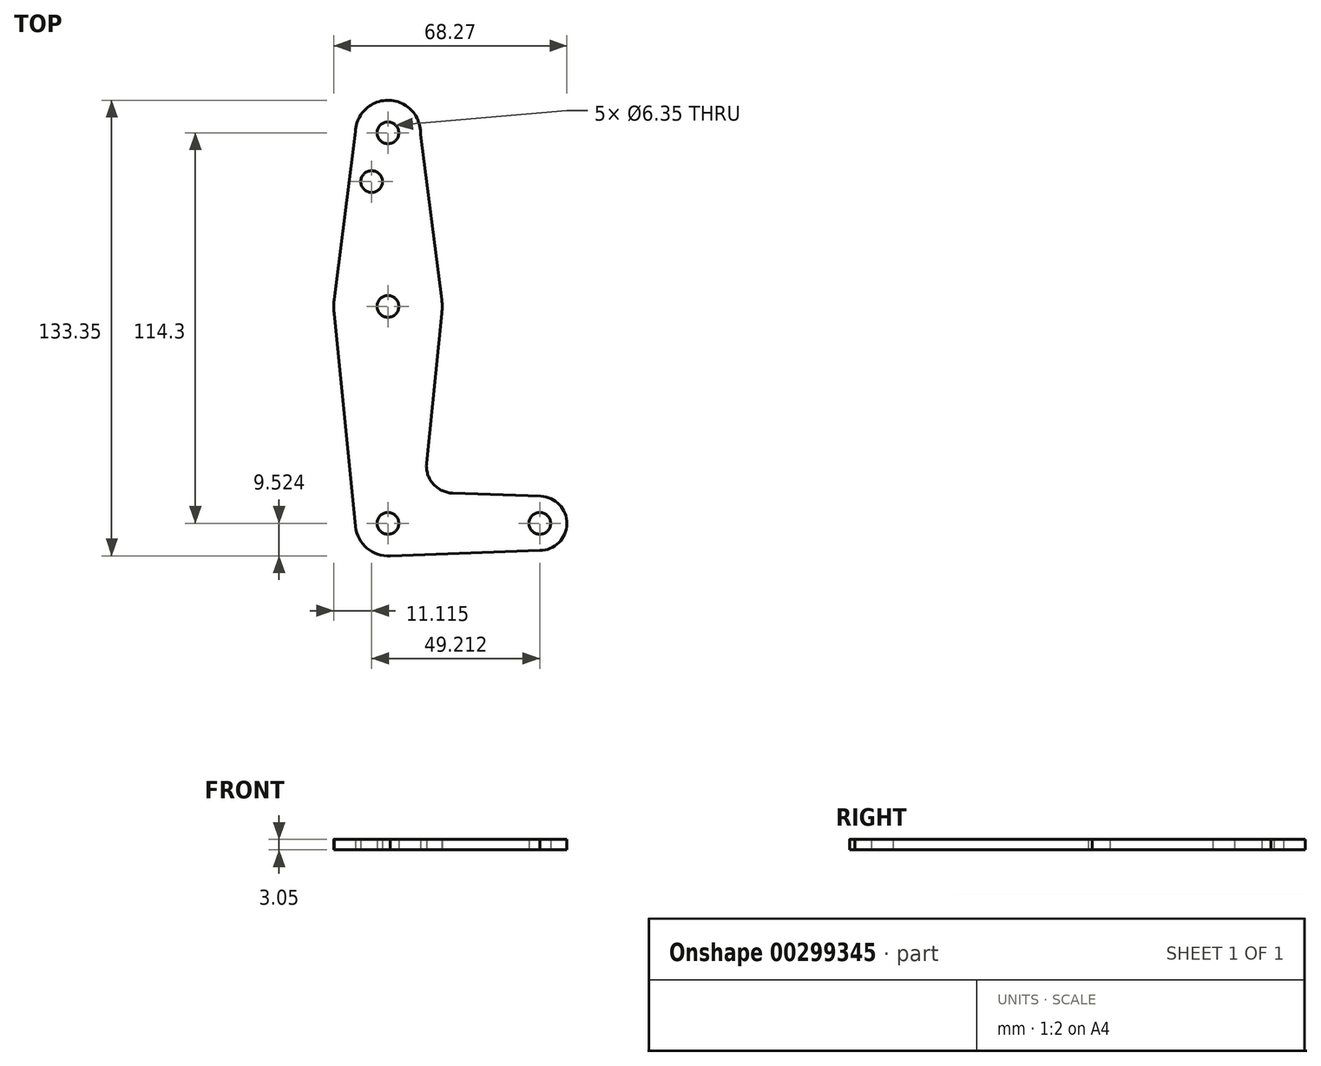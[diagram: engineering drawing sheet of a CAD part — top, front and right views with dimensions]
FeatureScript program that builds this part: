
annotation { "Feature Type Name" : "Feature", "Feature Type Description" : "" }
export const myFeature = defineFeature(function(context is Context, id is Id, definition is map)
    precondition{}
    {
        {
            var Q0;
            Q0=qCreatedBy(makeId("Top.planeOp"),FACE);
            var sketch = newSketch(context, id + "F0", { "sketchPlane" : qUnion([Q0])});
            skLineSegment(sketch, "E0", {"start": v(-11.27, 77.32) * mm, "end": v(-11.27, -36.98) * mm, "construction": true});
            skLineSegment(sketch, "E1", {"start": v(-11.27, -36.98) * mm, "end": v(33.18, -36.98) * mm, "construction": true});
            skCircle(sketch, "E2", {"center": v(-11.27, 77.32) * mm, "radius": 9.53 * mm});
            skCircle(sketch, "E3", {"center": v(-11.27, 26.52) * mm, "radius": 15.88 * mm});
            skCircle(sketch, "E4", {"center": v(-11.27, -36.98) * mm, "radius": 9.53 * mm});
            skCircle(sketch, "E5", {"center": v(33.18, -36.98) * mm, "radius": 7.94 * mm});
            skLineSegment(sketch, "E6", {"start": v(-11.27, -46.5) * mm, "end": v(33.18, -44.91) * mm});
            skCircle(sketch, "E7", {"center": v(-11.27, 77.32) * mm, "radius": 3.18 * mm});
            skCircle(sketch, "E8", {"center": v(-11.27, 26.52) * mm, "radius": 3.18 * mm});
            skCircle(sketch, "E9", {"center": v(-11.27, -36.98) * mm, "radius": 3.18 * mm});
            skCircle(sketch, "E10", {"center": v(33.18, -36.98) * mm, "radius": 3.18 * mm});
            skCircle(sketch, "E11", {"center": v(-16.03, 63.05) * mm, "radius": 3.18 * mm});
            skPoint(sketch, "E12.newPointA", {"position": v(0, -26.21) * mm});
            skLineSegment(sketch, "E13", {"start": v(-1.76, 76.8) * mm, "end": v(4.47, 28.56) * mm});
            skLineSegment(sketch, "E14", {"start": v(4.47, 28.56) * mm, "end": v(4.47, 24.49) * mm});
            skLineSegment(sketch, "E15", {"start": v(4.47, 24.49) * mm, "end": v(0.03, -19.38) * mm});
            skLineSegment(sketch, "E16", {"start": v(-20.79, 77.73) * mm, "end": v(-27.02, 28.52) * mm});
            skLineSegment(sketch, "E17", {"start": v(-27.02, 28.52) * mm, "end": v(-27.02, 24.53) * mm});
            skLineSegment(sketch, "E18", {"start": v(-27.02, 24.53) * mm, "end": v(-20.75, -37.93) * mm});
            skLineSegment(sketch, "E19", {"start": v(7.66, -28.13) * mm, "end": v(33.46, -29.04) * mm});
            skPoint(sketch, "E20.newPointA", {"position": v(-1.75, -36.98) * mm});
            skArc(sketch, "E20.filletArc", {"start": v(0.03, -19.38) * mm, "mid": v(1.95, -25.4) * mm, "end": v(7.66, -28.13) * mm});
            skSolve(sketch);
        }
        {
            var Q0;
            Q0 = qSketchRegion(id + "F0", true);
            extrude(context, id + "F1", {"entities" : qUnion([Q0]), "depth" : 3.05 * mm});
        }
    });
